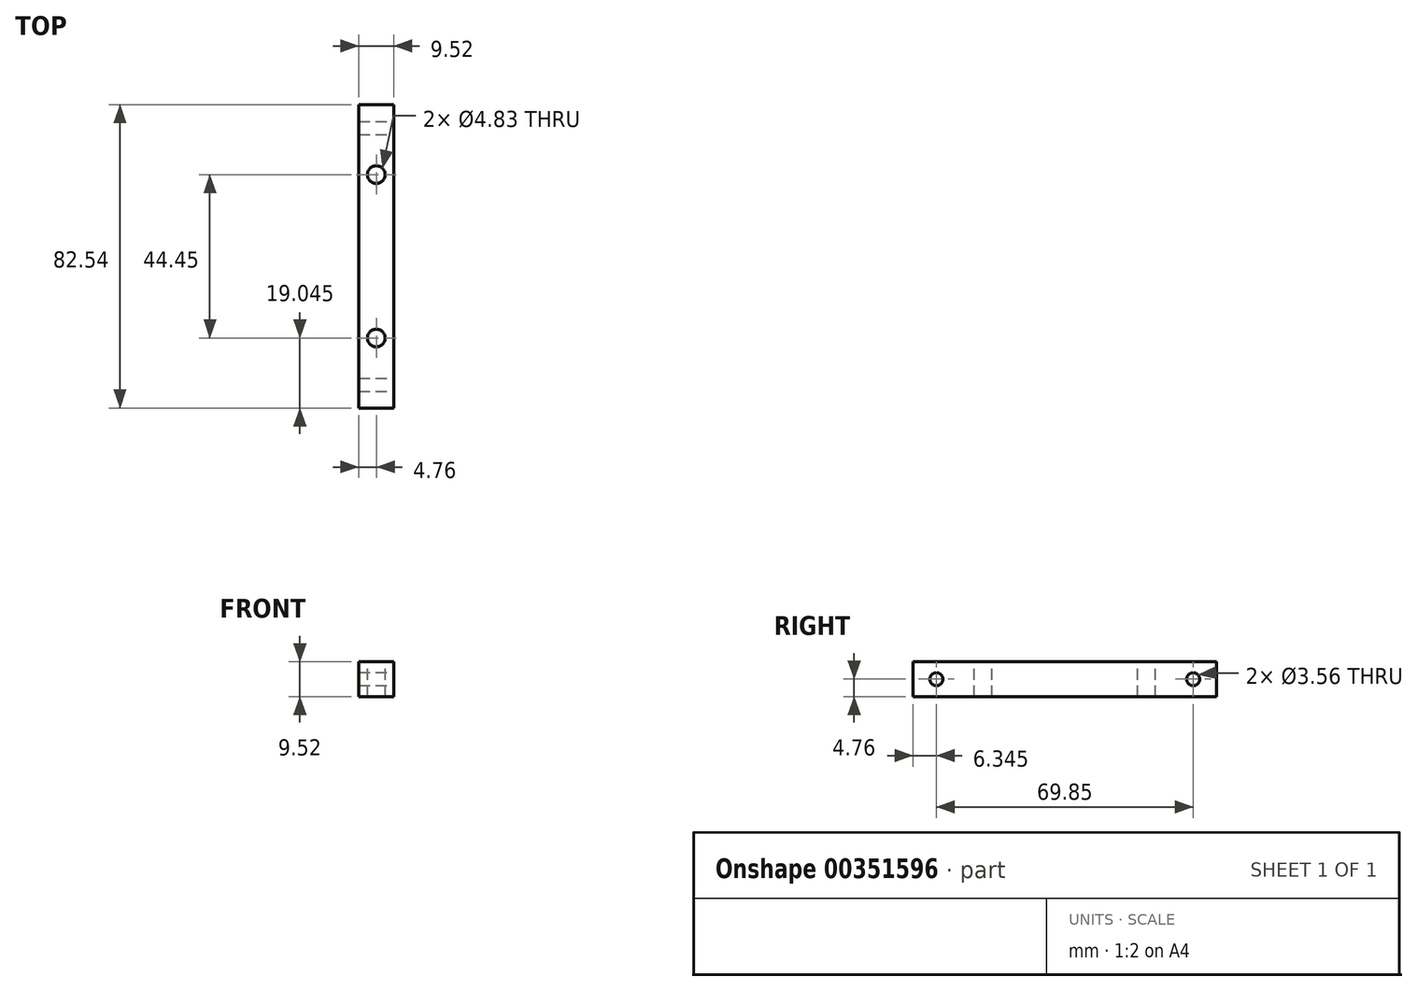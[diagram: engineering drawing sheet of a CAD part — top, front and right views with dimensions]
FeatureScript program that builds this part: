
annotation { "Feature Type Name" : "Feature", "Feature Type Description" : "" }
export const myFeature = defineFeature(function(context is Context, id is Id, definition is map)
    precondition{}
    {
        {
            var Q0;
            Q0=qCreatedBy(makeId("Front.planeOp"),FACE);
            var sketch = newSketch(context, id + "F0", { "sketchPlane" : qUnion([Q0])});
            skLineSegment(sketch, "E0.bottom", {"start": v(4.76, 4.76) * mm, "end": v(-4.76, 4.76) * mm});
            skLineSegment(sketch, "E0.top", {"start": v(4.76, -4.76) * mm, "end": v(-4.76, -4.76) * mm});
            skLineSegment(sketch, "E0.left", {"start": v(4.76, 4.76) * mm, "end": v(4.76, -4.76) * mm});
            skLineSegment(sketch, "E0.right", {"start": v(-4.76, 4.76) * mm, "end": v(-4.76, -4.76) * mm});
            skPoint(sketch, "E0.middle", {"position": v(0, 0) * mm});
            skSolve(sketch);
        }
        {
            var Q0;
            Q0 = qSketchRegion(id + "F0", true);
            extrude(context, id + "F1", {"entities" : qUnion([Q0]), "depth" : 82.55 * mm, "symmetric" : true});
        }
        {
            var Q0;
            Q0=makeQuery(id+"F1.opExtrude","SWEPT_FACE",FACE,{"disambiguationData":[OSD([sQuery(id+"F0.wireOp",EDGE,"E0.left")])]});
            var sketch = newSketch(context, id + "F2", { "sketchPlane" : qUnion([Q0])});
            skCircle(sketch, "E1", {"center": v(-34.93, 0) * mm, "radius": 1.78 * mm});
            skSolve(sketch);
        }
        {
            var Q0;
            Q0 = qSketchRegion(id + "F2", true);
            extrude(context, id + "F3", {"entities" : qUnion([Q0]), "operationType" : NewBodyOperationType.REMOVE, "endBound" : BoundingType.THROUGH_ALL, "oppositeDirection" : true, "depth" : 25.4 * mm});
        }
        {
            var Q0;
            Q0=makeQuery(id+"F1.opExtrude","SWEPT_FACE",FACE,{"disambiguationData":[OSD([sQuery(id+"F0.wireOp",EDGE,"E0.left")])]});
            var sketch = newSketch(context, id + "F4", { "sketchPlane" : qUnion([Q0])});
            skCircle(sketch, "E2", {"center": v(34.93, 0) * mm, "radius": 1.78 * mm});
            skSolve(sketch);
        }
        {
            var Q0;
            Q0 = qSketchRegion(id + "F4", true);
            extrude(context, id + "F5", {"entities" : qUnion([Q0]), "operationType" : NewBodyOperationType.REMOVE, "endBound" : BoundingType.THROUGH_ALL, "oppositeDirection" : true, "depth" : 25.4 * mm});
        }
        {
            var Q0;
            Q0=makeQuery(id+"F1.opExtrude","SWEPT_FACE",FACE,{"disambiguationData":[OSD([sQuery(id+"F0.wireOp",EDGE,"E0.bottom")])]});
            var sketch = newSketch(context, id + "F6", { "sketchPlane" : qUnion([Q0])});
            skCircle(sketch, "E3", {"center": v(0, -22.23) * mm, "radius": 2.41 * mm});
            skSolve(sketch);
        }
        {
            var Q0;
            Q0 = qSketchRegion(id + "F6", true);
            extrude(context, id + "F7", {"entities" : qUnion([Q0]), "operationType" : NewBodyOperationType.REMOVE, "endBound" : BoundingType.THROUGH_ALL, "oppositeDirection" : true, "depth" : 25.4 * mm});
        }
        {
            var Q0;
            Q0=makeQuery(id+"F1.opExtrude","SWEPT_FACE",FACE,{"disambiguationData":[OSD([sQuery(id+"F0.wireOp",EDGE,"E0.bottom")])]});
            var sketch = newSketch(context, id + "F8", { "sketchPlane" : qUnion([Q0])});
            skCircle(sketch, "E4", {"center": v(0, 22.23) * mm, "radius": 2.41 * mm});
            skSolve(sketch);
        }
        {
            var Q0;
            Q0 = qSketchRegion(id + "F8", true);
            extrude(context, id + "F9", {"entities" : qUnion([Q0]), "operationType" : NewBodyOperationType.REMOVE, "endBound" : BoundingType.THROUGH_ALL, "oppositeDirection" : true, "depth" : 25.4 * mm});
        }
    });
